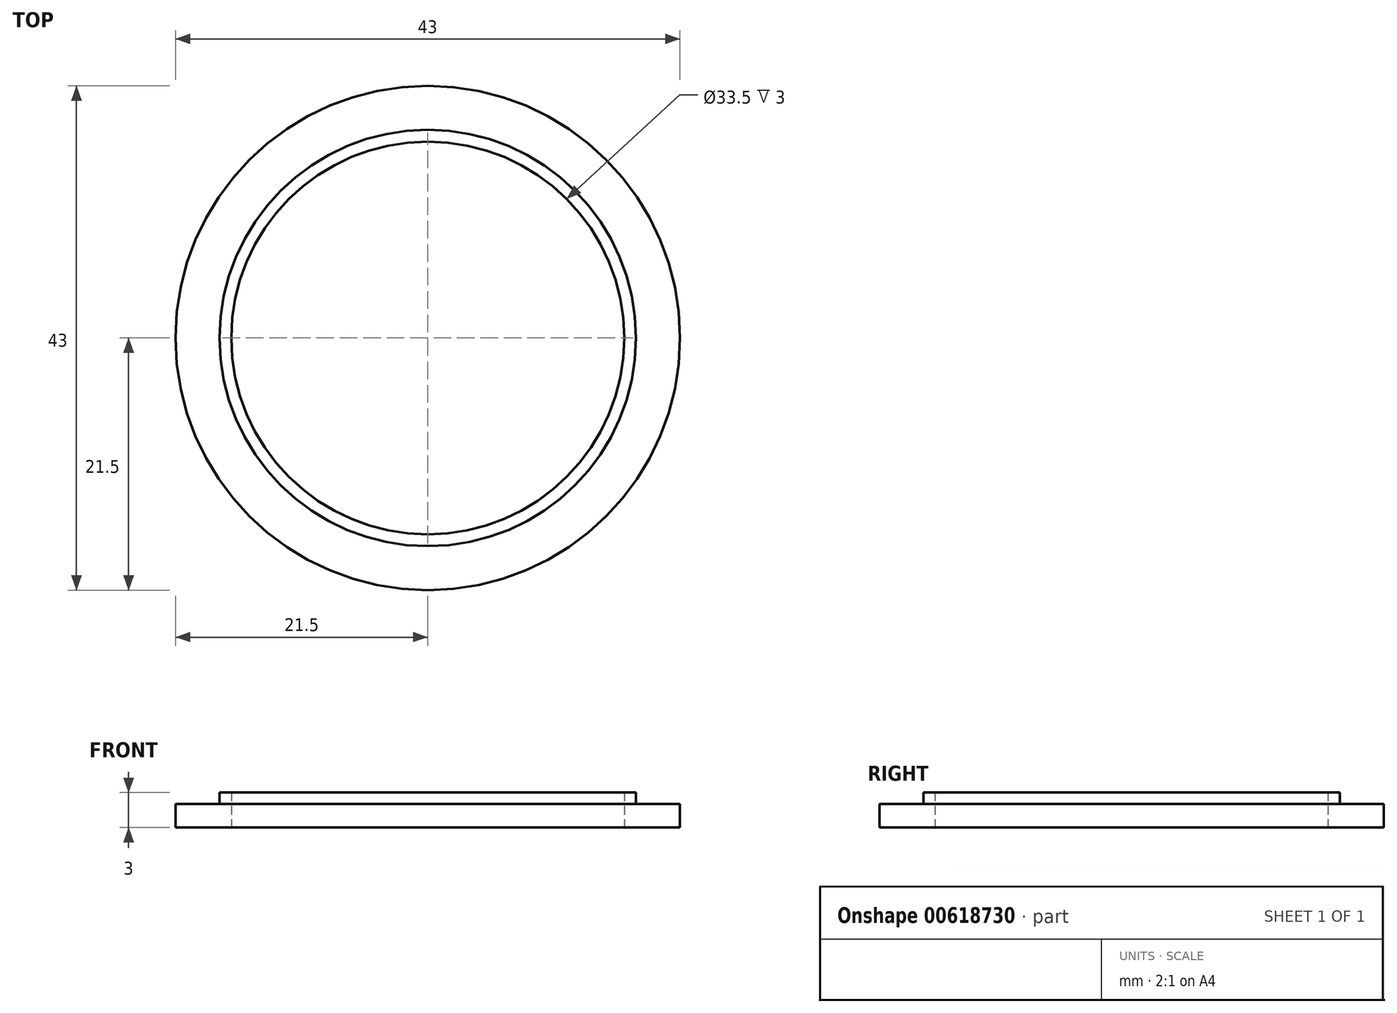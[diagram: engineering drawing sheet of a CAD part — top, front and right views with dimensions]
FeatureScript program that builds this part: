
annotation { "Feature Type Name" : "Feature", "Feature Type Description" : "" }
export const myFeature = defineFeature(function(context is Context, id is Id, definition is map)
    precondition{}
    {
        {
            var Q0;
            Q0=qCreatedBy(makeId("Top.planeOp"),FACE);
            var sketch = newSketch(context, id + "F0", { "sketchPlane" : qUnion([Q0])});
            skCircle(sketch, "E0", {"center": v(0, 0) * mm, "radius": 21.5 * mm});
            skCircle(sketch, "E1", {"center": v(0, 0) * mm, "radius": 16.75 * mm});
            skSolve(sketch);
        }
        {
            var Q0;
            Q0 = qSketchRegion(id + "F0", true);
            extrude(context, id + "F1", {"entities" : qUnion([Q0]), "depth" : 2 * mm, "offsetDistance" : 25 * mm});
        }
        {
            var Q0;
            Q0=makeQuery(id+"F1.opExtrude","CAP_FACE",FACE,{"disambiguationData":[OSD([sQuery(id+"F0.wireOp",EDGE,"E0"),sQuery(id+"F0.wireOp",EDGE,"E1")])],"isStart":false});
            var sketch = newSketch(context, id + "F2", { "sketchPlane" : qUnion([Q0])});
            skCircle(sketch, "E2", {"center": v(0, 0) * mm, "radius": 16.75 * mm});
            skCircle(sketch, "E3", {"center": v(0, 0) * mm, "radius": 17.75 * mm});
            skPoint(sketch, "E4", {"position": v(0, 16.75) * mm});
            skPoint(sketch, "E5", {"position": v(0, 17.75) * mm});
            skSolve(sketch);
        }
        {
            var Q0;
            Q0 = qSketchRegion(id + "F2", true);
            extrude(context, id + "F3", {"entities" : qUnion([Q0]), "operationType" : NewBodyOperationType.ADD, "depth" : 1 * mm, "offsetDistance" : 25 * mm});
        }
    });
